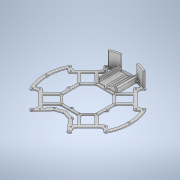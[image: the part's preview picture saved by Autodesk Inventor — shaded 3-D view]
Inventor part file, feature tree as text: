
AUTODESK INVENTOR PART (.ipt)
format: ipt  version: 2020 (Build 240168000, 168)  size: 1,554,432 bytes
history: native  units: mm
features: projected_geometry x25, extrude x17, sketch x11, other x4, fillet x3, chamfer x1
ambient origin geometry x8: Origin, YZ Plane, XZ Plane, XY Plane, X Axis, Y Axis, Z Axis, Center Point
bodies: Body1 (feature_tree)
feature tree (61):
  other  "Твердое тело1"
  extrude  "outer"  TaperAngle=45.0deg  [1 undecoded]
  extrude  "inner"  Depth=7.0mm
  sketch  "Эскиз3"
  extrude  "Выдавливание3"  Depth=20.0mm
  extrude  "Выдавливание4"  Depth=7.0mm
  sketch  "Эскиз4"
  extrude  "Выдавливание5"  Depth=3.2mm
  extrude  "Выдавливание6"  Depth=59.0mm
  sketch  "Эскиз5"
  extrude  "Выдавливание7"  Depth=83.0mm
  extrude  "Выдавливание8"  Depth=69.0mm
  sketch  "Эскиз6"
  extrude  "Выдавливание9"  Depth=55.0mm
  extrude  "Выдавливание10"  Depth=3.0mm
  other  "РабПлоскость1"
  extrude  "Выдавливание11"  Depth=8.0mm
  chamfer  "Фаска1"  Distance=5.0mm
  fillet  "Сопряжение1"  Radius=2.0mm
  fillet  "Сопряжение2"  Radius=40.0mm
  other  "РабПлоскость2"
  extrude  "Выдавливание12"  Depth=2.0mm
  sketch  "Эскиз9"
  extrude  "Выдавливание13"  Depth=105.0mm
  extrude  "Выдавливание14"  Depth=2.0mm
  other  "РабПлоскость3"
  extrude  "Выдавливание15"  Depth=2.0mm TaperAngle=0.0deg
  extrude  "Выдавливание16"  Depth=3.5mm
  fillet  "Сопряжение3"  Radius=2.0mm
  extrude  "Выдавливание17"  Depth=6.0mm
  sketch  "Эскиз1"
  sketch  "Эскиз2"
  projected_geometry  "Спроецированная петля1"
  projected_geometry  "Спроецированная петля2"
  projected_geometry  "Спроецированная петля3"
  projected_geometry  "Спроецированная петля4"
  projected_geometry  "Спроецированная петля5"
  sketch  "Эскиз7"
  projected_geometry  "Спроецированная петля6"
  projected_geometry  "Спроецированная петля7"
  projected_geometry  "Спроецированная петля8"
  sketch  "Эскиз8"
  projected_geometry  "Спроецированная петля9"
  projected_geometry  "Спроецированная петля10"
  projected_geometry  "Спроецированная петля11"
  projected_geometry  "Спроецированная петля12"
  projected_geometry  "Спроецированная петля13"
  projected_geometry  "Спроецированная петля14"
  projected_geometry  "Спроецированная петля15"
  sketch  "Эскиз10"
  projected_geometry  "Спроецированная петля16"
  projected_geometry  "Спроецированная петля17"
  projected_geometry  "Спроецированная петля18"
  projected_geometry  "Спроецированная петля19"
  projected_geometry  "Спроецированная петля20"
  projected_geometry  "Спроецированная петля21"
  projected_geometry  "Спроецированная петля22"
  projected_geometry  "Спроецированная петля23"
  projected_geometry  "Спроецированная петля24"
  projected_geometry  "Спроецированная петля25"
  sketch  "Эскиз11"
note: 1 required parameter value undecoded (feature->parameter linkage not recoverable at this tier; creation-order binding heuristic only, values carry confidence <= 0.55)
